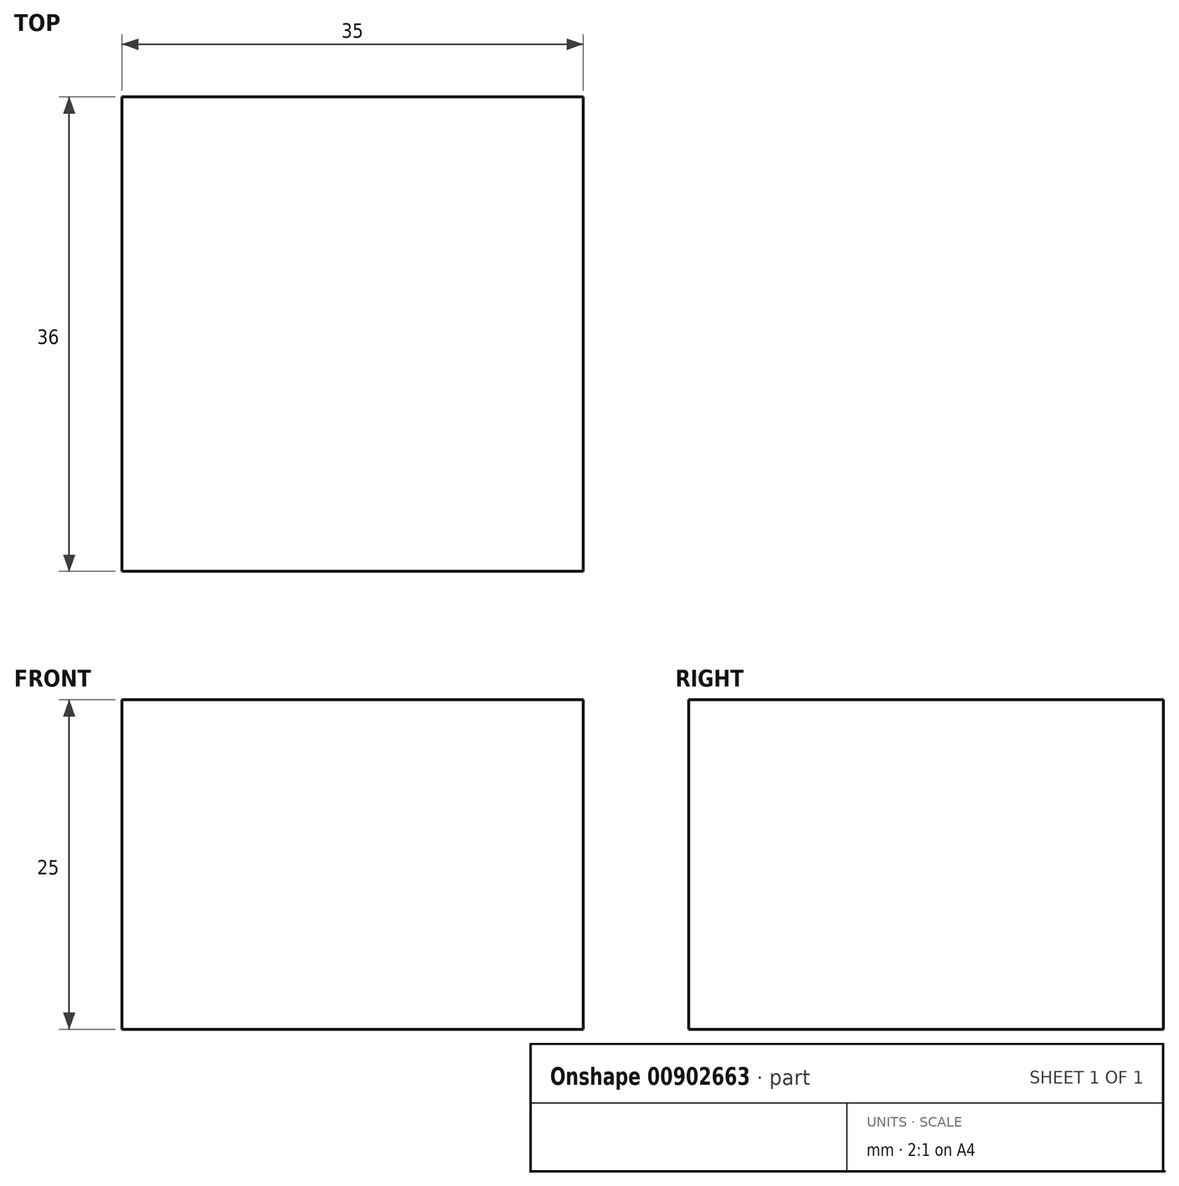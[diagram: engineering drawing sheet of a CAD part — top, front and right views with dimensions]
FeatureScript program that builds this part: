
annotation { "Feature Type Name" : "Feature", "Feature Type Description" : "" }
export const myFeature = defineFeature(function(context is Context, id is Id, definition is map)
    precondition{}
    {
        {
            var Q0;
            Q0=qCreatedBy(makeId("Top.planeOp"),FACE);
            var sketch = newSketch(context, id + "F0", { "sketchPlane" : qUnion([Q0])});
            skLineSegment(sketch, "E0.bottom", {"start": v(-10, 18) * mm, "end": v(25, 18) * mm});
            skLineSegment(sketch, "E0.top", {"start": v(-10, -18) * mm, "end": v(25, -18) * mm});
            skLineSegment(sketch, "E0.left", {"start": v(-10, 18) * mm, "end": v(-10, -18) * mm});
            skLineSegment(sketch, "E0.right", {"start": v(25, 18) * mm, "end": v(25, -18) * mm});
            skSolve(sketch);
        }
        {
            var Q0;
            Q0 = qSketchRegion(id + "F0", true);
            extrude(context, id + "F1", {"entities" : qUnion([Q0]), "depth" : -25 * mm, "offsetDistance" : 25 * mm});
        }
    });
